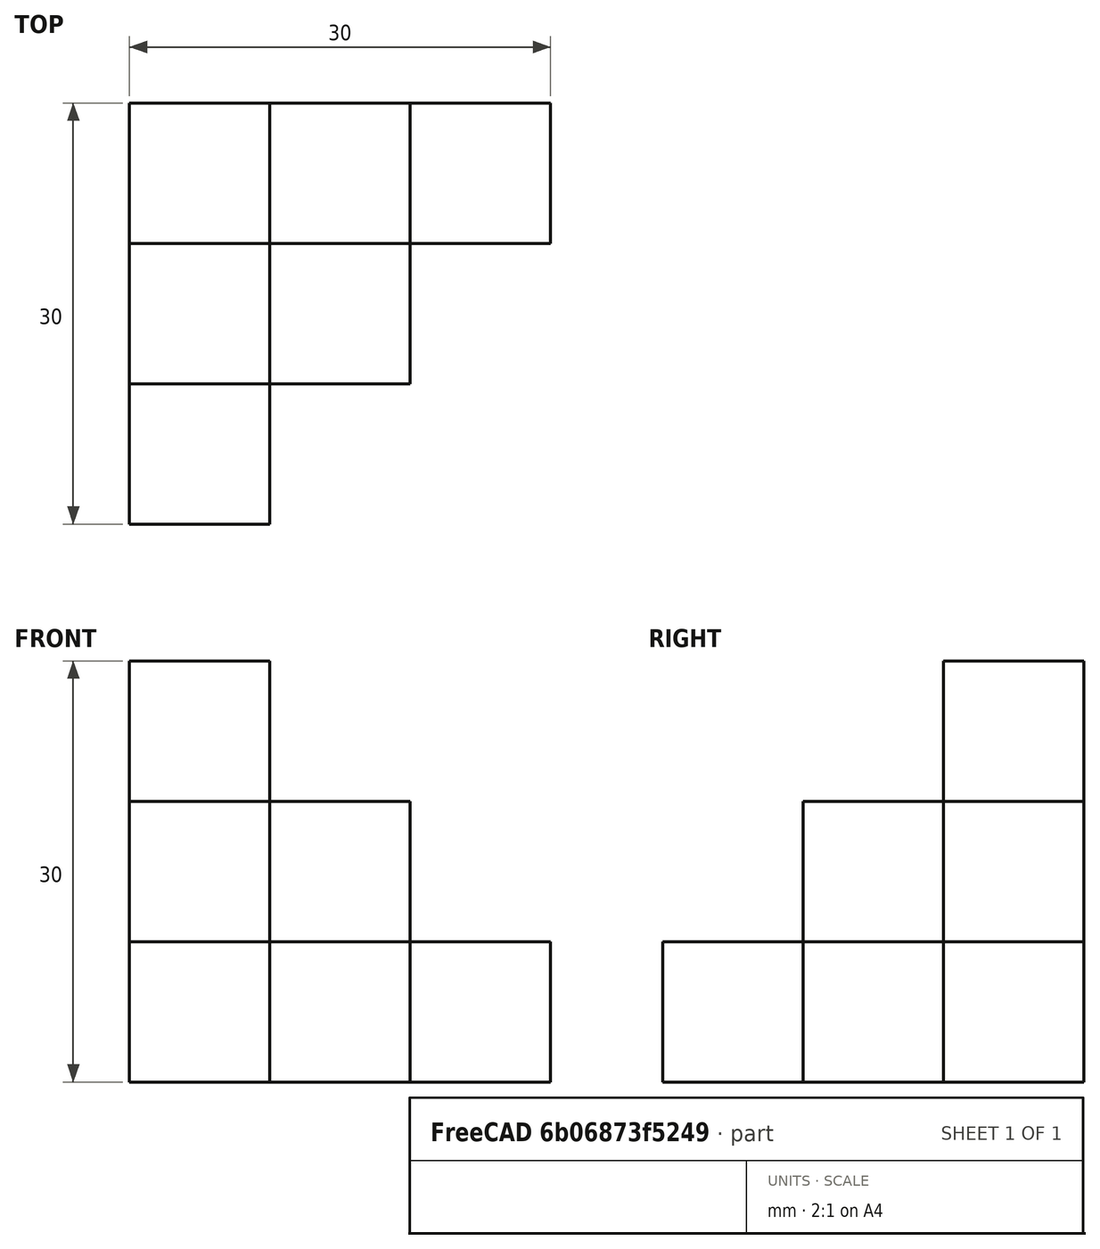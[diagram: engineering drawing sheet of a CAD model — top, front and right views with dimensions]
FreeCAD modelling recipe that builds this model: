
FCSTD DOCUMENT  (FreeCAD 1.0R39319 (Git))
Label: ojt1_t04r01_qbert 3 levels
License: All rights reserved
LicenseURL: https://en.wikipedia.org/wiki/All_rights_reserved
objects: Part::Box×6
note: 6 computed .brp shape members not serialized (recipe doc carries the construction recipe); baked Part::Feature solids carry a one-line shape summary decoded from their .brp

FEATURE [Part::Box] Box  label="Cube"
  AttacherType = Attacher::AttachEngine3D
  Height = 30
  Length = 10
  Width = 10
FEATURE [Part::Box] Box001  label="Cube001"
  AttacherType = Attacher::AttachEngine3D
  Height = 20
  Length = 10
  Placement = pos=(10,0,0) rot=(0,0,1;0rad)
  Width = 10
FEATURE [Part::Box] Box002  label="Cube002"
  AttacherType = Attacher::AttachEngine3D
  Height = 20
  Length = 10
  Placement = pos=(0,-10,0) rot=(0,0,1;0rad)
  Width = 10
FEATURE [Part::Box] Box003  label="Cube003"
  AttacherType = Attacher::AttachEngine3D
  Height = 10
  Length = 10
  Placement = pos=(10,-10,0) rot=(0,0,1;0rad)
  Width = 10
FEATURE [Part::Box] Box004  label="Cube004"
  AttacherType = Attacher::AttachEngine3D
  Height = 10
  Length = 10
  Placement = pos=(20,0,0) rot=(0,0,1;0rad)
  Width = 10
FEATURE [Part::Box] Box005  label="Cube005"
  AttacherType = Attacher::AttachEngine3D
  Height = 10
  Length = 10
  Placement = pos=(0,-20,0) rot=(0,0,1;0rad)
  Width = 10
